FCSTD DOCUMENT  (FreeCAD 1.0R39109 (Git))
Label: Master Document
License: All rights reserved
LicenseURL: http://en.wikipedia.org/wiki/All_rights_reserved
objects: Spreadsheet::Sheet×1

FEATURE [Spreadsheet::Sheet] Spreadsheet  label="Monitor Chassis Parameters"
  cells = A1='Parameter Name; B1='Value; C1='Notes; A2='GSWallHalfLength; B2(GSWallHalfLength)==B58; C2='Does not include outer radius portion of the wall, only the rectangular part; A3='GSBottomWallHeight; B3(GSBottomWallHeight)==B88 + B105 + B11; A4='GSWallWidth; B4(GSWallWidth)=123; A5='GSBaseFloorBeamWidth; B5(GSBaseFloorBeamWidth)==B33 * 3; C5='Is relelative to the size of the screw hole size; A6='GSBaseBodyThickness; B6(GSBaseBodyThickness)=3; A7='GSCamWallThickness; B7(GSCamWallThickness)=4; A8='GSThinWallThickness; B8(GSThinWallThickness)=3; A9='GSCamWallClickIndent; B9(GSCamWallClickIndent)=1; A10='GSCamWallClickLength; B10(GSCamWallClickLength)=6; A11='GSCamWallFullClickStructureHeight; B11(GSCamWallFullClickStructureHeight)=20; A14='GSCamBoardHeight; B14(GSCamBoardHeight)=38; A15='GSCamBoardWidth; B15(GSCamBoardWidth)=38; A16='GSCamBoardMountingHoleDiameter; B16(GSCamBoardMountingHoleDiameter)==B43; A17='GSCamPlateThickness; B17(GSCamPlateThickness)=4; A18='GSCamMountingHoleOffset; B18(GSCamMountingHoleOffset)=4; A19='GSCamMountingHoleThickness; B19(GSCamMountingHoleThickness)=2; A20='GSCamMountingHoleHeight; B20(GSCamMountingHoleHeight)=7; A21='GSCamAxisHoleDiameter; B21(GSCamAxisHoleDiameter)==B44; C21='M4 uses a 4.5 mm hole; A22='GSCamAxisWidth; B22(GSCamAxisWidth)=22; A23='GSCamMountingIndentInnerDiameter; B23(GSCamMountingIndentInnerDiameter)=5; C23='TBD - Not a good name?; A24='GSCamMountingHoleDiameter; B24(GSCamMountingHoleDiameter)=2.5; A25='GSCamGimbalDepth; B25(GSCamGimbalDepth)=20; A26='GSCam1ZAxisSetback; B26(GSCam1ZAxisSetback)=15; C26='The camera will be mounted back, away from the lens to help the tilt ability; A27='GSCam2ZAxisSetback; B27(GSCam2ZAxisSetback)=15; C27='The camera will be mounted back, away from the lens to help the tilt ability; A28='GSCamGimbalLighteningSlotOffsetFromCenter; B28(GSCamGimbalLighteningSlotOffsetFromCenter)=12; A29='GSCamGimbalInnerLength; B29(GSCamGimbalInnerLength)=58; A30='GSCam1GimbalHoleHeight; B30(GSCam1GimbalHoleHeight)=50; A31='GSCam2GimbalHoleHeight; B31(GSCam2GimbalHoleHeight)=35; A32='GSCamM4NutHexagonDiameter; B32(GSCamM4NutHexagonDiameter)=8.4; A33='GSCamM4ScrewHoleDiameter; B33(GSCamM4ScrewHoleDiameter)=3.3; A34='GSM4CountersunkScrewHoleDiameter; B34(GSM4CountersunkScrewHoleDiameter)=4.5; A35='GSCamM4NutDepth; B35(GSCamM4SNutDepth)=4; A36='GSCamM3NutDepth; B36(GSCamM3NutDepth)=3.5; A37='GSCamM5NutHexagonDiameter; B37(GSCamM5NutHexagonDiameter)=9.5; A38='GSCamM3NutHexagonDiameter; B38(GSCamM3NutHexagonDiameter)=6.6; A39='GSCamM5ScrewHoleDiameter; B39(GSCamM5ScrewHoleDiameter)=5.5; A40='GSCamM5NutDepth; B40(GSCamM5NutDepth)=4; A41='GSLEDPowerRiserHeight; B41(GSLEDPowerRiserHeight)=7; A42='GSM3BoltHoleDiameter; B42(GSM3BoltHoleDiameter)=3.4; A43='GSM25BoltHoleDiameter; B43(GSM25BoltHoleDiameter)=2.9; A44='GSM4BoltHoleDiameter; B44(GSM4BoltHoleDiameter)=4.5; A45='GSM4BoltHeadIndentDiameter; B45(GSM4BoltHeadIndentDiameter)=7.5; A46='GSM4BoltCountersinkDiameter; B46(GSM4BoltCountersinkDiameter)=8; A47='GSM3BoltCountersinkDiameter; B47(GSM3BoltCountersinkDiameter)=5.3; A48='GSM2BoltCountersinkDiameter; B48(GSM2BoltCountersinkDiameter)=3.5; A50='GSM2TappingScrewHoleDiameter; B50(GSM2TappingScrewHoleDiameter)=1.71; A51='GSM2_5TappingScrewHoleDiameter; B51(GSM2_5TappingScrewHoleDiameter)=2.05; A52='GSM3TappingScrewHoleDiameter; B52(GSM3TappingScrewHoleDiameter)=2.4; A53='GSM4TappingScrewHoleDiameter; B53(GSM4TappingScrewHoleDiameter)=3.4; A55='GSMonitorFloorPowerBayLength; B55(GSMonitorFloorPowerBayLength)=155; A57='GSMonitorFloorWidth_PiSide; B57(GSMonitorFloorWidth_PiSide)==B4 - 2 * B8; A58='GSMonitorFloorLength_PiSide; B58(GSMonitorFloorLength_PiSide)=170; A59='GSMonitorCameraBayLength; B59(GSMonitorCameraBayLength)=130; C59='TBD - May not use.  Instead, just have a single right- and left- number so that the viewports are the same?; F59='Total Inner Length; G59==B59 + B64 + B65 + B75; A60='GSMonitorStrobeBayLength; B60(GSMonitorStrobeBayLength)=130; C60='TBD - Not used; A61='GSMonitorViewPortLengthRight; B61(GSMonitorViewPortLengthRight)=100; A62='GSMonitorViewPortLengthLeft; B62(GSMonitorViewPortLengthLeft)=50; A64='GSMonitorPiBayLength; B64(GSMonitorPiBayLength)=100; A65='GSMonitorExtraBayLength; B65(GSMonitorExtraBayLength)=10; A66='GSMonitorFloorThickness; B66(GSMonitorFloorThickness)=4; A67='GSMonitorFloorPiSideLengthShare; B67(GSMonitorFloorPiSideLengthShare)=30; C67='This amount of the Pi-side is moved to the Power side to share the overall length to fit on printer; A68='GSMonitorFloorJointOverlap; B68(GSMonitorFloorJointOverlap)=14; A69='GSMonitorFloorPiEndOffset; B69(GSMonitorFloorPiEndOffset)=32; C69='Offset from end of floor rectangle (not rounded part) to nearest Pi board mounting hole; A70='GSMonitorFloorPiNearSideOffset; B70(GSMonitorFloorPiNearSideOffset)=51; C70='Offset from camera side of inner wall to the Pi 5 mounting screw; A71='GSMonitorFloorMountHoleSideOffset; B71(GSMonitorFloorMountHoleSideOffset)=8; C71='From inner side to the hole that the floor will be screwed into; A72='GSMonitorFloorMountHoleSideOffsetForWall; B72(GSMonitorFloorMountHoleSideOffsetForWall)==B71 - 1; C72='TBD - Fix so that a separate value here is not needed.  Needed because wall measures the side offset from the lip, not the  same place the Floor does.; A73='GSM5ScrewHoleDiameter; B73(GSM5ScrewHoleDiameter)=3.3; A74='GSMonitorFloorMountHoleEdgeOffset; B74(GSMonitorFloorMountHoleEdgeOffset)=8; C74='From edge (e.g., from the side or the middle of the floors) back to the screw that will mount to the wall; A75='GSMonitorFloorPowerBayLength; B75=150; A76='GSMonitorFloorMountingScrewDiameter; B76(GSMonitorFloorMountingScrewDiameter)=2.5; C76='2.4 is nominal, but that was a little tight in PLA; A77='GSMonitorFloorRibMinimumWidth; B77(GSMonitorFloorRibMinimumWidth)=10; A78='GSMonitorFloorMountingScrewDepth; B78(GSMonitorFloorMountingScrewDepth)=6; A79='GSMonitorWallTensionReliefCutWidth; B79(GSMonitorWallTensionReliefCutWidth)=0.5; A80='GSMonitorWallHalfConnectionBoltDiameter; B80(GSMonitorWallHalfConnectionBoltDiameter)==B42; A81='GSMonitorPowerFloorJointScrewEdgeOffset; B81(GSMonitorPowerFloorJointScrewEdgeOffset)=8; A83='GSPi5MountingHoleCenterLength; B83(GSPi5MountingHoleCenterLength)=58; A84='GsPi5MountingHoleCenterWidth; B84(GSPi5MountingHoleCenterWidth)=49; A85='GsPi5MountingHoleDiameter; B85(GsPi5MountingHoleDiameter)=3; A86='GsPi5NetworkSideBoardLength; B86(GsPi5NetworkSideBoardLength)=22; C86='Length from the edge of the nearest mounting hole to the side of the board that has the network connector on it; A87='GSPi5MountingRiserHeight; B87(GSPi5MountingRiserHeight)=4; A88='GSPi5FullHeightInclConnectorsAndFloor; B88(GSPi5FullHeightInclConnectorsAndFloor)=60; A90='GSMonitorFloorCameraMountHoleDiameter; B90(GSMonitorFloorCameraMountHoleDiameter)==B39; A91='GSMonitorFloorCamera1_MountHoleFrontOffset; B91(GSMonitorFloorCamera1_MountHoleFrontOffset)=56; C91='Critical, as must be far enough back to avoid lense hitting front of enclosure, but close enough to allow good down-angling; A92='GSMonitorFloorCamera2_MountHoleFrontOffset; B92(GSMonitorFloorCamera2_MountHoleFrontOffset)=50; A93='GSMonitorFloorCameraMountHoleEdgeOffset; B93(GSMonitorFloorCameraMountHoleEdgeOffset)=155; C93='Offset from outer (right) edge - TBD - is this in use?; A94='GSMonitorFloorCamera1MountHoleEdgeOffsetFromCenter; B94(GSMonitorFloorCamera1MountHoleEdgeOffsetFromCenter)=23; C94='TBD - Need smaller gimbal dimensions to make this fit; A95='GSMonitorFloorCamera2MountHoleEdgeOffsetFromCenter; B95(GSMonitorFloorCamera2MountHoleEdgeOffsetFromCenter)=25; A97='GSMonitorFloorStrobeMountHoleDiameter; B97(GSMonitorFloorStrobeMountHoleDiameter)==B39; A98='GSMonitorFloorStrobeMountHoleFrontOffset; B98(GSMonitorFloorStrobeMountHoleFrontOffset)=30; +515 more cells
